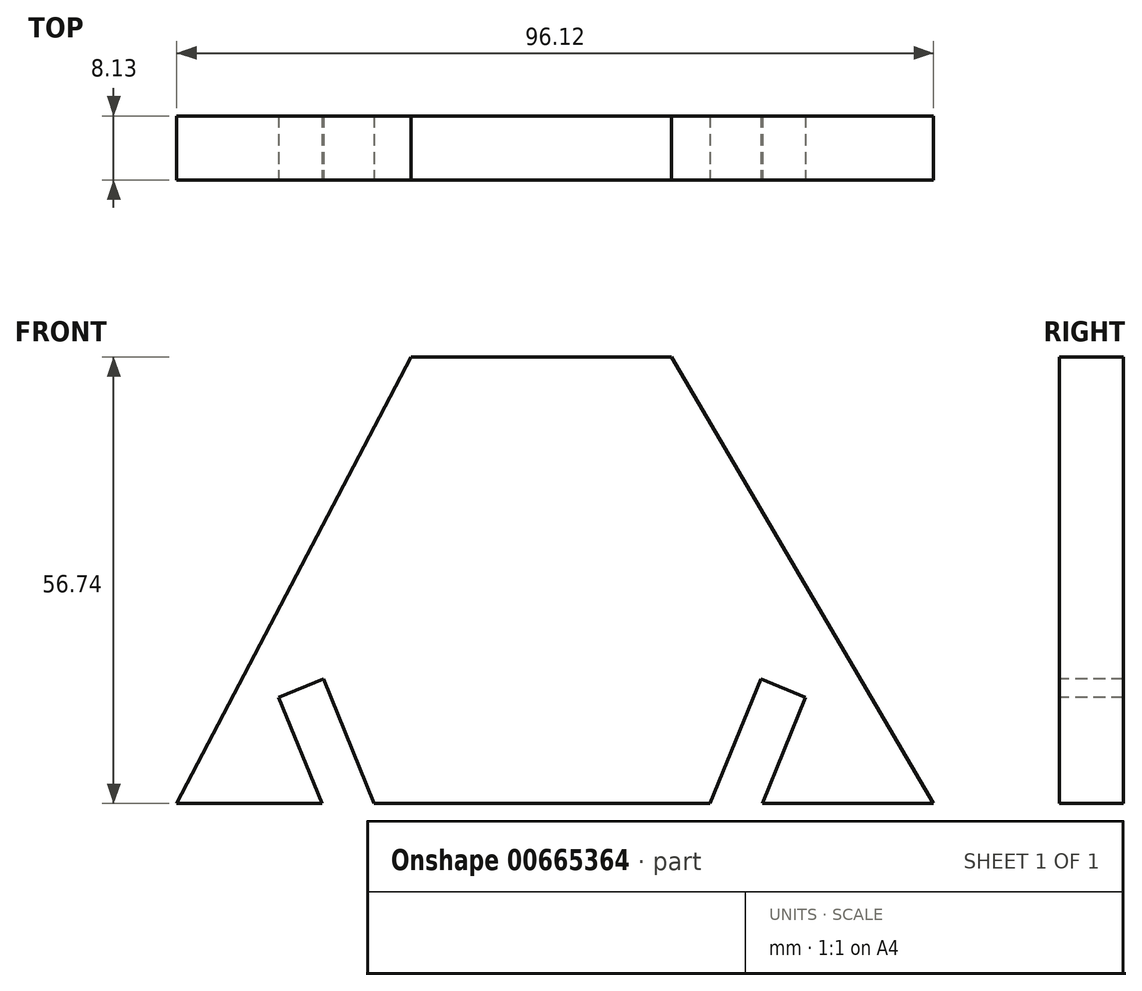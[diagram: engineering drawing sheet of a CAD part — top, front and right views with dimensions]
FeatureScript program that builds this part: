
annotation { "Feature Type Name" : "Feature", "Feature Type Description" : "" }
export const myFeature = defineFeature(function(context is Context, id is Id, definition is map)
    precondition{}
    {
        {
            var Q0;
            Q0=qCreatedBy(makeId("Front.planeOp"),FACE);
            var sketch = newSketch(context, id + "F0", { "sketchPlane" : qUnion([Q0])});
            skLineSegment(sketch, "E0", {"start": v(-46.4, 0) * mm, "end": v(-16.66, 56.74) * mm});
            skLineSegment(sketch, "E1", {"start": v(-16.66, 56.74) * mm, "end": v(16.4, 56.74) * mm});
            skLineSegment(sketch, "E2", {"start": v(16.4, 56.74) * mm, "end": v(49.71, 0) * mm});
            skLineSegment(sketch, "E3", {"start": v(-27.96, 0) * mm, "end": v(-33.46, 13.5) * mm});
            skLineSegment(sketch, "E4", {"start": v(-33.46, 13.5) * mm, "end": v(-27.78, 15.82) * mm});
            skLineSegment(sketch, "E5", {"start": v(-27.78, 15.82) * mm, "end": v(-21.32, 0) * mm});
            skLineSegment(sketch, "E6.MirrorCS", {"start": v(33.46, 13.5) * mm, "end": v(27.78, 15.82) * mm});
            skLineSegment(sketch, "E7.MirrorCS", {"start": v(27.96, 0) * mm, "end": v(33.46, 13.5) * mm});
            skLineSegment(sketch, "E8.MirrorCS", {"start": v(27.78, 15.82) * mm, "end": v(21.32, 0) * mm});
            skLineSegment(sketch, "E9", {"start": v(-27.96, 0) * mm, "end": v(-46.4, 0) * mm});
            skLineSegment(sketch, "E10", {"start": v(-21.32, 0) * mm, "end": v(21.32, 0) * mm});
            skLineSegment(sketch, "E11", {"start": v(27.96, 0) * mm, "end": v(49.71, 0) * mm});
            skSolve(sketch);
        }
        {
            var Q0;
            Q0=makeQuery(id+"F0.imprint","IMPRINT",FACE,{"disambiguationData":[TD([[makeQuery(id+"F0.imprint","IMPRINT",EDGE,{"derivedFrom":sQuery(id+"F0.wireOp",EDGE,"E0")}),-1.0]])]});
            extrude(context, id + "F1", {"entities" : qUnion([Q0]), "oppositeDirection" : true, "depth" : 8.13 * mm, "offsetDistance" : 25.4 * mm});
        }
    });
